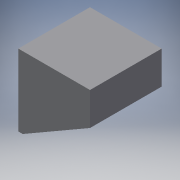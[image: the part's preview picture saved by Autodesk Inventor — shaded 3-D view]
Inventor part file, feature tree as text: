
AUTODESK INVENTOR PART (.ipt)
format: ipt  version: 2019 (Build 230136000, 136)  size: 109,056 bytes
history: native  units: in
note: dims shown in document units (in); Inventor stores cm internally (conversion verified against a paired STEP export)
features: extrude x2, sketch x2, projected_geometry x1
ambient origin geometry x8: Origin, YZ Plane, XZ Plane, XY Plane, X Axis, Y Axis, Z Axis, Center Point
bodies: Body1 (feature_tree)
feature tree (5):
  extrude  "Extrusion2"  Depth=0.125in
  extrude  "Extrusion3"  Depth=2.0in
  sketch  "Sketch2"  dims[d5=30.0deg d6=0.125in]
  sketch  "Sketch3"  dims[d7=2.0in d8=2.0in d9=2.0in d10=0.0in d11=1.5in d12=1.125in d13=0.5in d14=0.0in]
  projected_geometry  "Projected Loop1"
